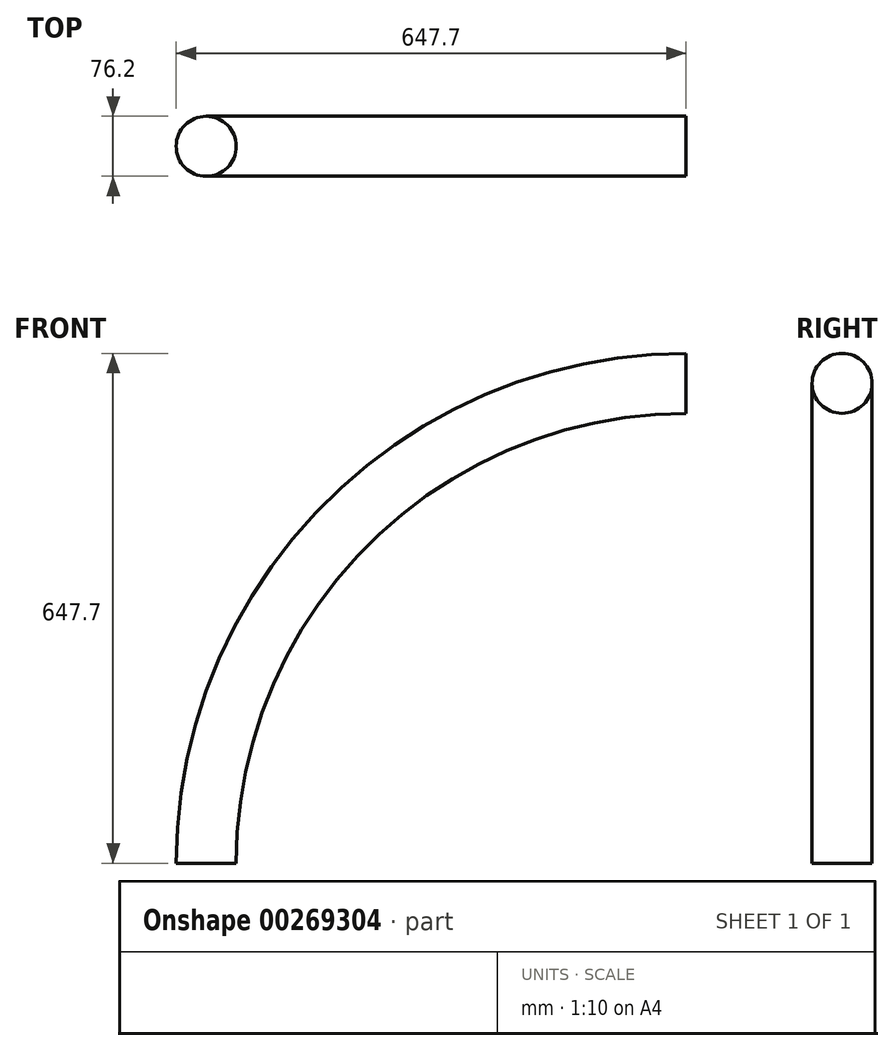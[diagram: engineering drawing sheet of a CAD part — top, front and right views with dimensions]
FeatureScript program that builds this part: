
annotation { "Feature Type Name" : "Feature", "Feature Type Description" : "" }
export const myFeature = defineFeature(function(context is Context, id is Id, definition is map)
    precondition{}
    {
        {
            var Q0;
            Q0=qCreatedBy(makeId("Front.planeOp"),FACE);
            var sketch = newSketch(context, id + "F0", { "sketchPlane" : qUnion([Q0])});
            skArc(sketch, "E0", {"start": v(-609.6, 0) * mm, "mid": v(-431.05, 431.05) * mm, "end": v(0, 609.6) * mm});
            skSolve(sketch);
        }
        {
            var Q0;
            Q0=qCreatedBy(makeId("Top.planeOp"),FACE);
            var sketch = newSketch(context, id + "F1", { "sketchPlane" : qUnion([Q0])});
            skCircle(sketch, "E1", {"center": v(-609.6, 0) * mm, "radius": 38.1 * mm});
            skSolve(sketch);
        }
        {
            var Q0;
            Q0=makeQuery(id+"F1.imprint","IMPRINT",FACE,{"disambiguationData":[TD([[makeQuery(id+"F1.imprint","IMPRINT",EDGE,{"derivedFrom":sQuery(id+"F1.wireOp",EDGE,"E1")}),1.0]])]});
            var Q1;
            Q1=sQuery(id+"F1.wireOp",EDGE,"E1");
            var Q2;
            Q2=sQuery(id+"F0.wireOp",EDGE,"E0");
            sweep(context, id + "F2", {"bodyType" : ToolBodyType.SURFACE, "profiles" : qUnion([Q0]), "surfaceProfiles" : qUnion([Q1]), "path" : qUnion([Q2])});
        }
    });
